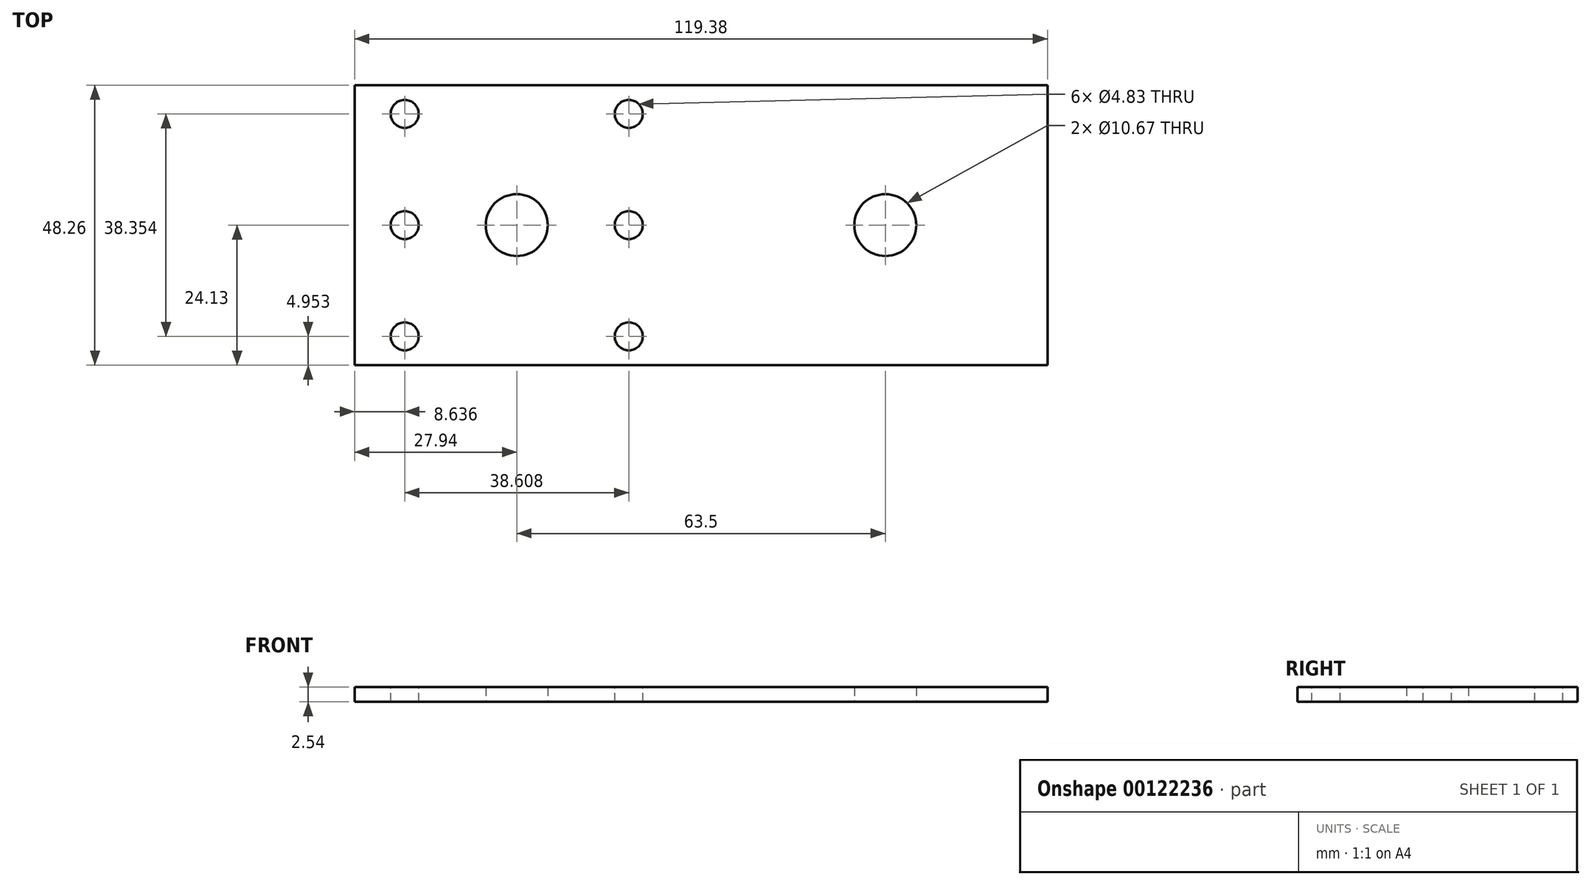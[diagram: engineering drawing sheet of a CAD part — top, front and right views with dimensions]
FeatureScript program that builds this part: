
annotation { "Feature Type Name" : "Feature", "Feature Type Description" : "" }
export const myFeature = defineFeature(function(context is Context, id is Id, definition is map)
    precondition{}
    {
        {
            var Q0;
            Q0=qCreatedBy(makeId("Top.planeOp"),FACE);
            var sketch = newSketch(context, id + "F0", { "sketchPlane" : qUnion([Q0])});
            skLineSegment(sketch, "E0.bottom", {"start": v(59.7, -24.13) * mm, "end": v(-59.7, -24.13) * mm});
            skLineSegment(sketch, "E0.top", {"start": v(59.7, 24.13) * mm, "end": v(-59.7, 24.13) * mm});
            skLineSegment(sketch, "E0.left", {"start": v(59.7, -24.13) * mm, "end": v(59.7, 24.13) * mm});
            skLineSegment(sketch, "E0.right", {"start": v(-59.7, -24.13) * mm, "end": v(-59.7, 24.13) * mm});
            skPoint(sketch, "E0.middle", {"position": v(0, 0) * mm});
            skCircle(sketch, "E1", {"center": v(31.75, 0) * mm, "radius": 5.33 * mm});
            skCircle(sketch, "E2", {"center": v(-31.75, 0) * mm, "radius": 5.33 * mm});
            skSolve(sketch);
        }
        {
            var Q0;
            Q0 = qSketchRegion(id + "F0", true);
            extrude(context, id + "F1", {"entities" : qUnion([Q0]), "depth" : 2.54 * mm});
        }
        {
            var Q0;
            Q0 = qSketchRegion(id + "F0", true);
            extrude(context, id + "F2", {"entities" : qUnion([Q0]), "operationType" : NewBodyOperationType.ADD, "depth" : 2.54 * mm});
        }
        {
            var Q0;
            Q0=makeQuery(id+"F1.opExtrude","CAP_FACE",FACE,{"disambiguationData":[OSD([sQuery(id+"F0.wireOp",EDGE,"E0.bottom"),sQuery(id+"F0.wireOp",EDGE,"E0.top"),sQuery(id+"F0.wireOp",EDGE,"E0.left"),sQuery(id+"F0.wireOp",EDGE,"E0.right"),sQuery(id+"F0.wireOp",EDGE,"E1"),sQuery(id+"F0.wireOp",EDGE,"E2")])],"isStart":false});
            var sketch = newSketch(context, id + "F3", { "sketchPlane" : qUnion([Q0])});
            skCircle(sketch, "E3", {"center": v(-51.05, 0) * mm, "radius": 2.41 * mm});
            skCircle(sketch, "E4", {"center": v(-51.05, 19.18) * mm, "radius": 2.41 * mm});
            skCircle(sketch, "E5", {"center": v(-51.05, -19.18) * mm, "radius": 2.41 * mm});
            skSolve(sketch);
        }
        {
            var Q0;
            Q0 = qSketchRegion(id + "F3", true);
            extrude(context, id + "F4", {"entities" : qUnion([Q0]), "operationType" : NewBodyOperationType.REMOVE, "endBound" : BoundingType.THROUGH_ALL, "oppositeDirection" : true, "depth" : 25.4 * mm});
        }
        {
            var Q0;
            Q0=makeQuery(id+"F1.opExtrude","CAP_FACE",FACE,{"disambiguationData":[OSD([sQuery(id+"F0.wireOp",EDGE,"E0.bottom"),sQuery(id+"F0.wireOp",EDGE,"E0.top"),sQuery(id+"F0.wireOp",EDGE,"E0.left"),sQuery(id+"F0.wireOp",EDGE,"E0.right"),sQuery(id+"F0.wireOp",EDGE,"E1"),sQuery(id+"F0.wireOp",EDGE,"E2")])],"isStart":false});
            var sketch = newSketch(context, id + "F5", { "sketchPlane" : qUnion([Q0])});
            skCircle(sketch, "E6", {"center": v(-12.45, 0) * mm, "radius": 2.41 * mm});
            skCircle(sketch, "E7", {"center": v(-12.45, 19.18) * mm, "radius": 2.41 * mm});
            skCircle(sketch, "E8", {"center": v(-12.45, -19.18) * mm, "radius": 2.41 * mm});
            skSolve(sketch);
        }
        {
            var Q0;
            Q0 = qSketchRegion(id + "F5", true);
            extrude(context, id + "F6", {"entities" : qUnion([Q0]), "operationType" : NewBodyOperationType.REMOVE, "endBound" : BoundingType.THROUGH_ALL, "oppositeDirection" : true, "depth" : 25.4 * mm});
        }
    });
